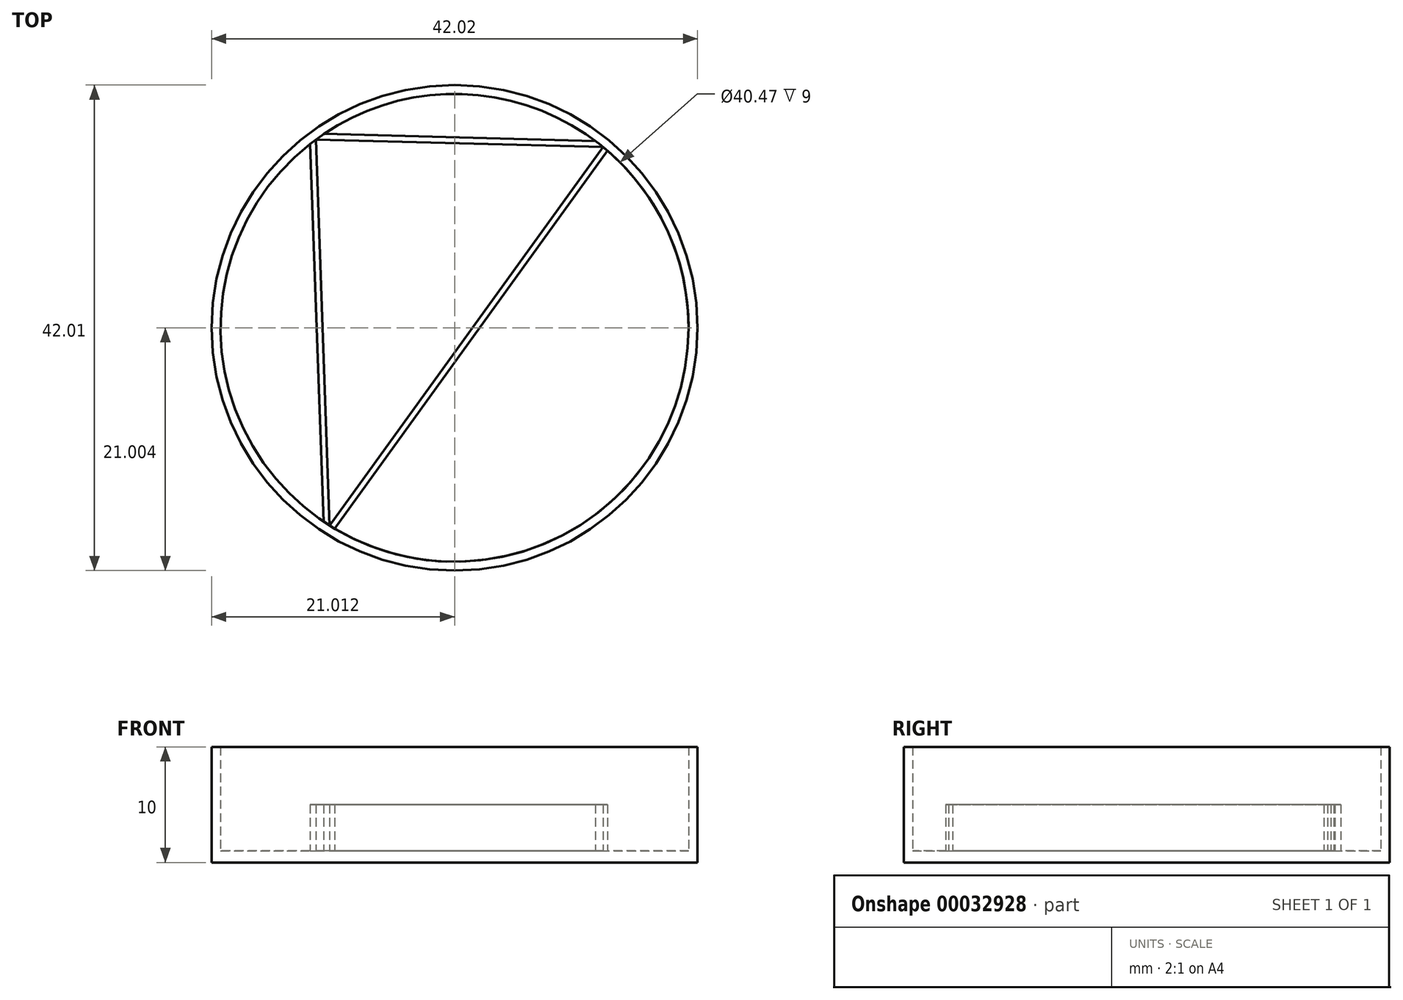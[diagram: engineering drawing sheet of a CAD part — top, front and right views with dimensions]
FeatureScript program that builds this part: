
annotation { "Feature Type Name" : "Feature", "Feature Type Description" : "" }
export const myFeature = defineFeature(function(context is Context, id is Id, definition is map)
    precondition{}
    {
        {
            var Q0;
            Q0=qCreatedBy(makeId("Top.planeOp"),FACE);
            var sketch = newSketch(context, id + "F0", { "sketchPlane" : qUnion([Q0])});
            skCircle(sketch, "E0", {"center": v(-22.27, 31.61) * mm, "radius": 20.23 * mm});
            skCircle(sketch, "E1.0", {"center": v(-22.27, 31.61) * mm, "radius": 21 * mm});
            skLineSegment(sketch, "E2", {"start": v(-34.27, 47.9) * mm, "end": v(-33.07, 14.5) * mm});
            skLineSegment(sketch, "E3", {"start": v(-33.07, 14.5) * mm, "end": v(-9.44, 47.26) * mm});
            skLineSegment(sketch, "E4", {"start": v(-9.44, 47.26) * mm, "end": v(-34.27, 47.9) * mm});
            skLineSegment(sketch, "E5.0", {"start": v(-10.1, 47.78) * mm, "end": v(-33.58, 48.39) * mm});
            skLineSegment(sketch, "E5.1", {"start": v(-32.64, 14.24) * mm, "end": v(-9.05, 46.94) * mm});
            skLineSegment(sketch, "E5.2", {"start": v(-34.76, 47.53) * mm, "end": v(-33.58, 14.84) * mm});
            skSolve(sketch);
        }
        {
            var Q0;
            Q0=makeQuery(id+"F0.imprint","IMPRINT",FACE,{"disambiguationData":[TD([[makeQuery(id+"F0.imprint","IMPRINT",EDGE,{"derivedFrom":sQuery(id+"F0.wireOp",EDGE,"E1.0")}),1.0]])]});
            extrude(context, id + "F1", {"entities" : qUnion([Q0]), "depth" : 10 * mm});
        }
        {
            var Q0;
            {var subQ1=sQuery(id+"F0.wireOp",EDGE,"E4");Q0=makeQuery(id+"F0.imprint","IMPRINT",FACE,{"disambiguationData":[TD([[makeQuery(id+"F0.imprint","IMPRINT",EDGE,{"derivedFrom":subQ1}),-1.0]])]});}
            var Q1;
            {var subQ1=sQuery(id+"F0.wireOp",EDGE,"E3");Q1=makeQuery(id+"F0.imprint","IMPRINT",FACE,{"disambiguationData":[TD([[makeQuery(id+"F0.imprint","IMPRINT",EDGE,{"derivedFrom":subQ1}),-1.0]])]});}
            var Q2;
            {var subQ1=sQuery(id+"F0.wireOp",EDGE,"E2");Q2=makeQuery(id+"F0.imprint","IMPRINT",FACE,{"disambiguationData":[TD([[makeQuery(id+"F0.imprint","IMPRINT",EDGE,{"derivedFrom":subQ1}),-1.0]])]});}
            extrude(context, id + "F2", {"entities" : qUnion([Q0, Q1, Q2]), "operationType" : NewBodyOperationType.ADD, "depth" : 5 * mm});
        }
        {
            var Q0;
            Q0=makeQuery(id+"F0.imprint","IMPRINT",FACE,{"disambiguationData":[TD([[makeQuery(id+"F0.imprint","IMPRINT",EDGE,{"derivedFrom":sQuery(id+"F0.wireOp",EDGE,"E2")}),1.0]])]});
            var Q1;
            {var subQ0=sQuery(id+"F0.wireOp",EDGE,"E5.0");Q1=makeQuery(id+"F0.imprint","IMPRINT",FACE,{"disambiguationData":[TD([[makeQuery(id+"F0.imprint","IMPRINT",EDGE,{"derivedFrom":subQ0}),-1.0]])]});}
            var Q2;
            {var subQ0=sQuery(id+"F0.wireOp",EDGE,"E5.1");Q2=makeQuery(id+"F0.imprint","IMPRINT",FACE,{"disambiguationData":[TD([[makeQuery(id+"F0.imprint","IMPRINT",EDGE,{"derivedFrom":subQ0}),-1.0]])]});}
            var Q3;
            {var subQ0=sQuery(id+"F0.wireOp",EDGE,"E5.2");Q3=makeQuery(id+"F0.imprint","IMPRINT",FACE,{"disambiguationData":[TD([[makeQuery(id+"F0.imprint","IMPRINT",EDGE,{"derivedFrom":subQ0}),-1.0]])]});}
            extrude(context, id + "F3", {"entities" : qUnion([Q0, Q1, Q2, Q3]), "operationType" : NewBodyOperationType.ADD, "depth" : 1 * mm});
        }
    });
